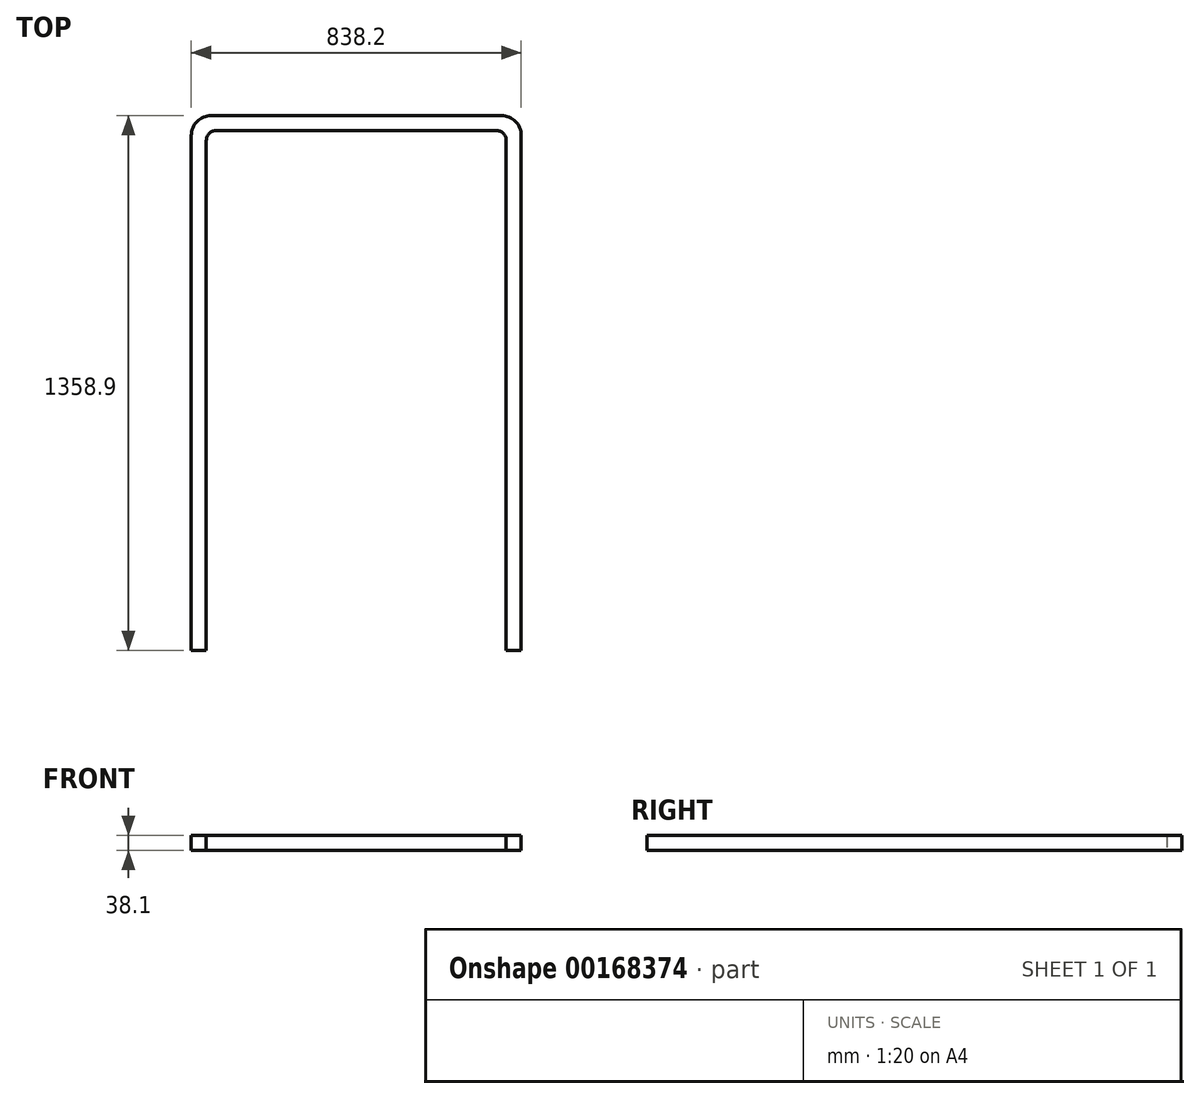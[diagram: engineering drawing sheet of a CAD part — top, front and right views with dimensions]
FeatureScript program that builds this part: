
annotation { "Feature Type Name" : "Feature", "Feature Type Description" : "" }
export const myFeature = defineFeature(function(context is Context, id is Id, definition is map)
    precondition{}
    {
        {
            var Q0;
            Q0=qCreatedBy(makeId("Top.planeOp"),FACE);
            var sketch = newSketch(context, id + "F0", { "sketchPlane" : qUnion([Q0])});
            skLineSegment(sketch, "E0.bottom", {"start": v(-481.27, 473.22) * mm, "end": v(255.33, 473.22) * mm});
            skLineSegment(sketch, "E0.left", {"start": v(-532.07, 422.42) * mm, "end": v(-532.07, -885.68) * mm});
            skLineSegment(sketch, "E0.right", {"start": v(306.13, 422.42) * mm, "end": v(306.13, -885.68) * mm});
            skPoint(sketch, "E0.middle", {"position": v(-112.97, -206.23) * mm});
            skLineSegment(sketch, "E1.top", {"start": v(-468.57, 435.12) * mm, "end": v(242.63, 435.12) * mm});
            skLineSegment(sketch, "E1.left", {"start": v(-493.97, -885.68) * mm, "end": v(-493.97, 409.72) * mm});
            skLineSegment(sketch, "E1.right", {"start": v(268.03, -885.68) * mm, "end": v(268.03, 409.72) * mm});
            skLineSegment(sketch, "E2", {"start": v(-532.07, -885.68) * mm, "end": v(-493.97, -885.68) * mm});
            skLineSegment(sketch, "E3", {"start": v(268.03, -885.68) * mm, "end": v(306.13, -885.68) * mm});
            skPoint(sketch, "E4.visualSharp", {"position": v(-532.07, 473.22) * mm});
            skArc(sketch, "E4.filletArc", {"start": v(-481.27, 473.22) * mm, "mid": v(-517.19, 458.34) * mm, "end": v(-532.07, 422.42) * mm});
            skPoint(sketch, "E5.visualSharp", {"position": v(-493.97, 435.12) * mm});
            skArc(sketch, "E5.filletArc", {"start": v(-468.57, 435.12) * mm, "mid": v(-486.53, 427.68) * mm, "end": v(-493.97, 409.72) * mm});
            skPoint(sketch, "E6.visualSharp", {"position": v(306.13, 473.22) * mm});
            skArc(sketch, "E6.filletArc", {"start": v(306.13, 422.42) * mm, "mid": v(291.25, 458.34) * mm, "end": v(255.33, 473.22) * mm});
            skPoint(sketch, "E7.visualSharp", {"position": v(268.03, 435.12) * mm});
            skArc(sketch, "E7.filletArc", {"start": v(268.03, 409.72) * mm, "mid": v(260.6, 427.68) * mm, "end": v(242.63, 435.12) * mm});
            skSolve(sketch);
        }
        {
            var Q0;
            Q0=makeQuery(id+"F0.imprint","IMPRINT",FACE,{"disambiguationData":[TD([[makeQuery(id+"F0.imprint","IMPRINT",EDGE,{"derivedFrom":sQuery(id+"F0.wireOp",EDGE,"E0.bottom")}),-1.0]])]});
            extrude(context, id + "F1", {"entities" : qUnion([Q0]), "depth" : 38.1 * mm});
        }
    });
